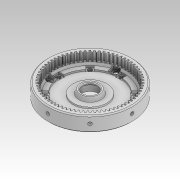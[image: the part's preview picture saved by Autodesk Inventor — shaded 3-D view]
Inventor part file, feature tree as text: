
AUTODESK INVENTOR PART (.ipt)
format: ipt  version: 2020 (Build 240168000, 168)  size: 1,839,616 bytes
history: native  units: mm
features: other x9, extrude x6, sketch x5, pattern_circular x4, chamfer x3, revolve x2, fillet x1, imported_body x1, projected_geometry x1
ambient origin geometry x8: Origin, YZ Plane, XZ Plane, XY Plane, X Axis, Y Axis, Z Axis, Center Point
bodies: Solid1 (feature_tree)
feature tree (32):
  other  "HD_mastersketch.ipt"
  other  "Blocks"
  revolve  "Revolution1"  [1 undecoded]
  extrude  "Extrusion1"  Depth=3.9mm
  extrude  "Extrusion3"  Depth=80.0mm TaperAngle=360.0deg
  pattern_circular  "Circular Pattern1"  [2 undecoded]
  extrude  "Extrusion2"  Depth=1.5mm
  fillet  "Fillet1"  Radius=700.0mm
  pattern_circular  "Circular Pattern2"  [2 undecoded]
  extrude  "Extrusion5"  Depth=1.5mm TaperAngle=0.0deg
  extrude  "Extrusion7"  Depth=1.5mm
  chamfer  "Chamfer1"  Distance=4.3mm
  extrude  "Extrusion8"  TaperAngle=0.0deg  [1 undecoded]
  chamfer  "Chamfer2"  Distance=2.268928mm
  pattern_circular  "Circular Pattern3"  [2 undecoded]
  revolve  "Revolution2"  [1 undecoded]
  pattern_circular  "Circular Pattern4"  Angle=45.0deg  [1 undecoded]
  chamfer  "Chamfer3"  Distance=8.726646mm
  other  "608 bearing"
  other  "Belt"
  other  "Rotor"
  imported_body  "Base"
  sketch  "Sketch5"  dims[d0=10.0mm d24=7.0mm d25=22.0mm d26=8.0mm]
  other  "M3NutDepth_bot"
  projected_geometry  "Projected Loop1"
  sketch  "Sketch7"  dims[d1=90.0deg d2=3.9mm]
  other  "BeltCutDepth_bot"
  sketch  "Sketch12"  dims[d4=4.0mm d5=0.0mm d6=80.0mm d7=360.0deg]
  sketch  "Sketch13"  dims[d9=0.8mm]
  sketch  "Sketch14"  dims[d11=1.8mm d12=4.0mm d13=0.0mm d14=0.45mm d15=700.0mm d16=360.0deg d18=5.7mm d19=4.0mm d20=0.0mm d29=47.0mm d30=4.3mm d31=0.0mm d32=0.0mm d38=2.268928mm d39=7.2mm d40=1.5mm d41=3.2mm d42=0.0mm d43=0.0mm d44=2.0mm d45=2.0mm d46=45.0deg d47=8.726646mm d48=0.523599mm d49=0.523599mm d50=0.523599mm d51=0.523599mm d52=0.523599mm d53=0.523599mm d56=2.792527mm d57=0.523599mm d58=68.0mm d59=70.740362mm d60=1.780032mm d61=9.749343mm d62=7.969311mm d63=6.189278mm d64=4.409246mm d65=2.629213mm d66=0.523599mm d67=0.523599mm d68=0.523599mm d69=0.523599mm d70=0.523599mm d72=11.529376mm d73=13.309408mm d74=15.089441mm d75=16.869473mm d76=18.649506mm d77=0.523599mm d78=0.523599mm d79=20.429538mm d80=22.209571mm d82=0.250579mm d83=72.932651mm d84=22.5mm d85=15.0mm d86=2.0mm d87=1.0mm d88=0.0mm d89=0.3mm d90=1.0mm d91=45.0deg d92=80.0mm d93=360.0deg d97=7.5mm d98=1.6mm d99=1.4mm d100=2.5mm d101=1.0mm d102=90.0deg d103=80.0mm d104=360.0deg d106=0.75mm d107=2.0mm d108=45.0deg]
  other  "608 bearing:1"
  other  "608 bearing:2"
note: 10 required parameter values undecoded (feature->parameter linkage not recoverable at this tier; creation-order binding heuristic only, values carry confidence <= 0.55)